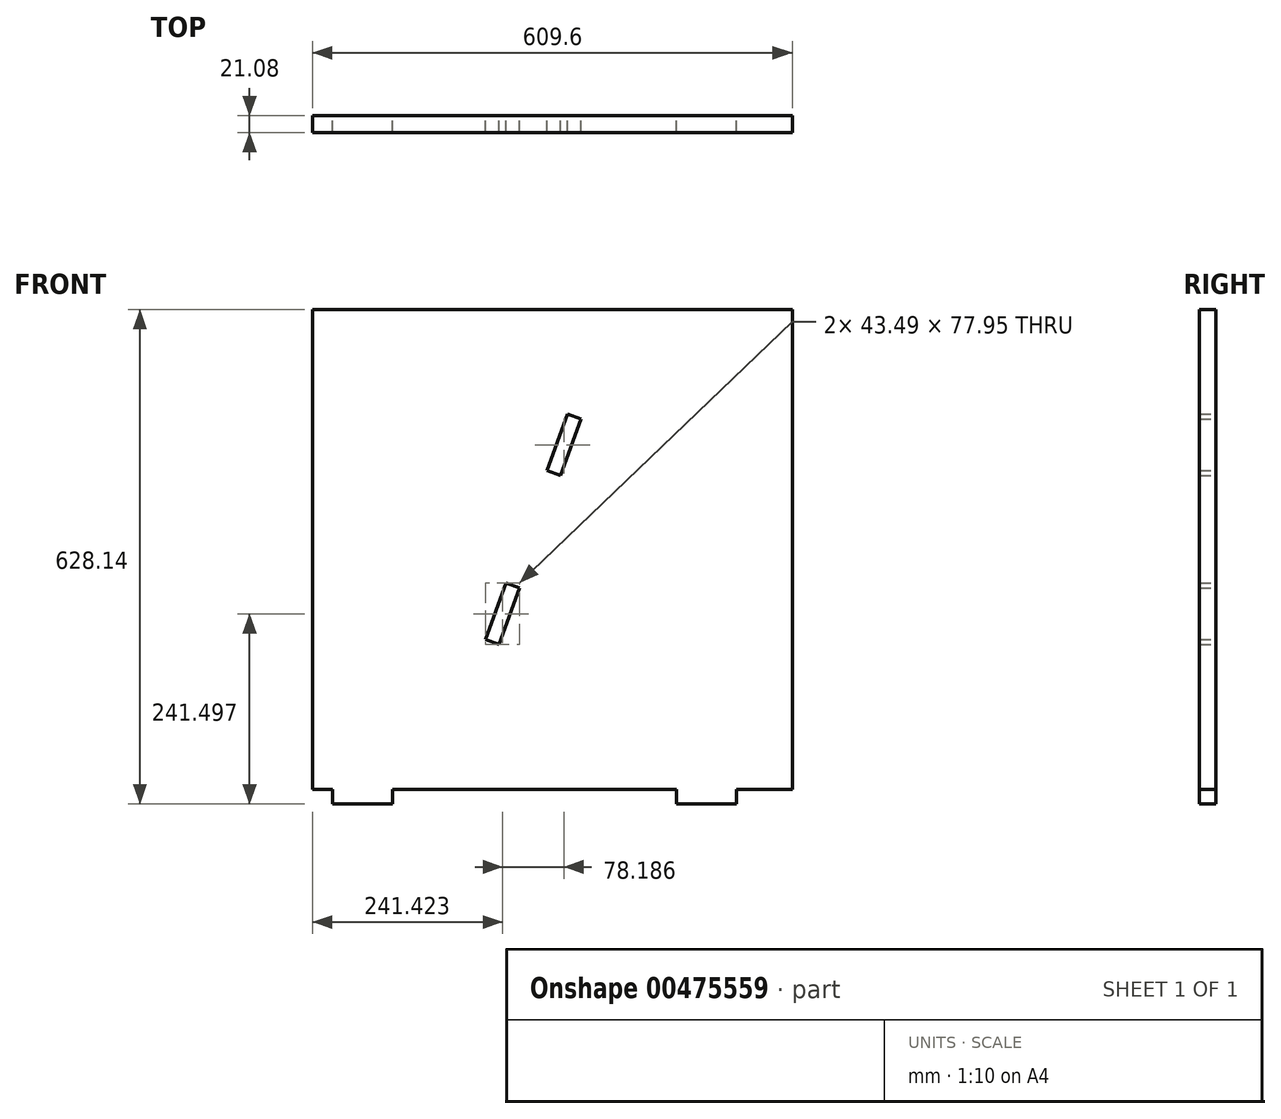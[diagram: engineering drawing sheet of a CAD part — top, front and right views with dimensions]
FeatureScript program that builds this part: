
annotation { "Feature Type Name" : "Feature", "Feature Type Description" : "" }
export const myFeature = defineFeature(function(context is Context, id is Id, definition is map)
    precondition{}
    {
        {
            var Q0;
            Q0=qCreatedBy(makeId("Front.planeOp"),FACE);
            var sketch = newSketch(context, id + "F0", { "sketchPlane" : qUnion([Q0])});
            skLineSegment(sketch, "E0.bottom", {"start": v(-219.68, 301.72) * mm, "end": v(389.92, 301.72) * mm});
            skLineSegment(sketch, "E0.top", {"start": v(-219.68, -307.88) * mm, "end": v(-194.28, -307.88) * mm});
            skLineSegment(sketch, "E0.left", {"start": v(-219.68, 301.72) * mm, "end": v(-219.68, -307.88) * mm});
            skLineSegment(sketch, "E0.right", {"start": v(389.92, 301.72) * mm, "end": v(389.92, -307.88) * mm});
            skLineSegment(sketch, "E1", {"start": v(-194.28, -307.88) * mm, "end": v(-194.28, -326.42) * mm});
            skLineSegment(sketch, "E2", {"start": v(-194.28, -326.42) * mm, "end": v(-118.08, -326.42) * mm});
            skLineSegment(sketch, "E3", {"start": v(-118.08, -326.42) * mm, "end": v(-118.08, -307.88) * mm});
            skLineSegment(sketch, "E4", {"start": v(-118.08, -307.88) * mm, "end": v(242.55, -307.88) * mm});
            skLineSegment(sketch, "E5", {"start": v(242.55, -307.88) * mm, "end": v(242.55, -326.42) * mm});
            skLineSegment(sketch, "E6", {"start": v(242.55, -326.42) * mm, "end": v(318.75, -326.42) * mm});
            skLineSegment(sketch, "E7", {"start": v(318.75, -326.42) * mm, "end": v(318.75, -307.88) * mm});
            skLineSegment(sketch, "E8", {"start": v(318.75, -307.88) * mm, "end": v(359.93, -307.88) * mm});
            skLineSegment(sketch, "E9.bottom", {"start": v(26.06, -45.95) * mm, "end": v(43.49, -52.3) * mm});
            skLineSegment(sketch, "E9.top", {"start": v(0, -117.55) * mm, "end": v(17.42, -123.9) * mm});
            skLineSegment(sketch, "E9.left", {"start": v(26.06, -45.95) * mm, "end": v(0, -117.55) * mm});
            skLineSegment(sketch, "E9.right", {"start": v(43.49, -52.3) * mm, "end": v(17.42, -123.9) * mm});
            skLineSegment(sketch, "E10.bottom", {"start": v(78.19, 97.26) * mm, "end": v(95.6, 90.92) * mm});
            skLineSegment(sketch, "E10.top", {"start": v(104.25, 168.86) * mm, "end": v(121.67, 162.52) * mm});
            skLineSegment(sketch, "E10.left", {"start": v(78.19, 97.26) * mm, "end": v(104.25, 168.86) * mm});
            skLineSegment(sketch, "E10.right", {"start": v(95.6, 90.92) * mm, "end": v(121.67, 162.52) * mm});
            skPoint(sketch, "E11.startSnap0", {"position": v(85.12, -307.88) * mm});
            skPoint(sketch, "E11.start.orphan", {"position": v(0, -307.88) * mm});
            skLineSegment(sketch, "E12.trimOffspring", {"start": v(318.75, -307.88) * mm, "end": v(389.92, -307.88) * mm});
            skSolve(sketch);
        }
        {
            var Q0;
            Q0=makeQuery(id+"F0.imprint","IMPRINT",FACE,{"disambiguationData":[TD([[makeQuery(id+"F0.imprint","IMPRINT",EDGE,{"derivedFrom":sQuery(id+"F0.wireOp",EDGE,"E0.bottom")}),-1.0]])]});
            extrude(context, id + "F1", {"entities" : qUnion([Q0]), "depth" : 2.54 * mm, "offsetDistance" : 25.4 * mm});
        }
        {
            var Q0;
            Q0=makeQuery(id+"F1.opExtrude","CAP_FACE",FACE,{"disambiguationData":[OSD([sQuery(id+"F0.wireOp",EDGE,"E0.bottom"),sQuery(id+"F0.wireOp",EDGE,"E0.left"),sQuery(id+"F0.wireOp",EDGE,"E0.right"),sQuery(id+"F0.wireOp",EDGE,"E0.top"),sQuery(id+"F0.wireOp",EDGE,"E1"),sQuery(id+"F0.wireOp",EDGE,"E2"),sQuery(id+"F0.wireOp",EDGE,"E3"),sQuery(id+"F0.wireOp",EDGE,"E5"),sQuery(id+"F0.wireOp",EDGE,"E6"),sQuery(id+"F0.wireOp",EDGE,"E7"),sQuery(id+"F0.wireOp",EDGE,"E9.bottom"),sQuery(id+"F0.wireOp",EDGE,"E9.top"),sQuery(id+"F0.wireOp",EDGE,"E9.left"),sQuery(id+"F0.wireOp",EDGE,"E9.right"),sQuery(id+"F0.wireOp",EDGE,"E10.bottom"),sQuery(id+"F0.wireOp",EDGE,"E10.top"),sQuery(id+"F0.wireOp",EDGE,"E10.left"),sQuery(id+"F0.wireOp",EDGE,"E10.right"),sQuery(id+"F0.wireOp",EDGE,"E12.trimOffspring"),sQuery(id+"F0.wireOp",EDGE,"E4")])],"isStart":false});
            extrude(context, id + "F2", {"entities" : qUnion([Q0]), "operationType" : NewBodyOperationType.ADD, "depth" : 18.54 * mm, "offsetDistance" : 25.4 * mm});
        }
    });
